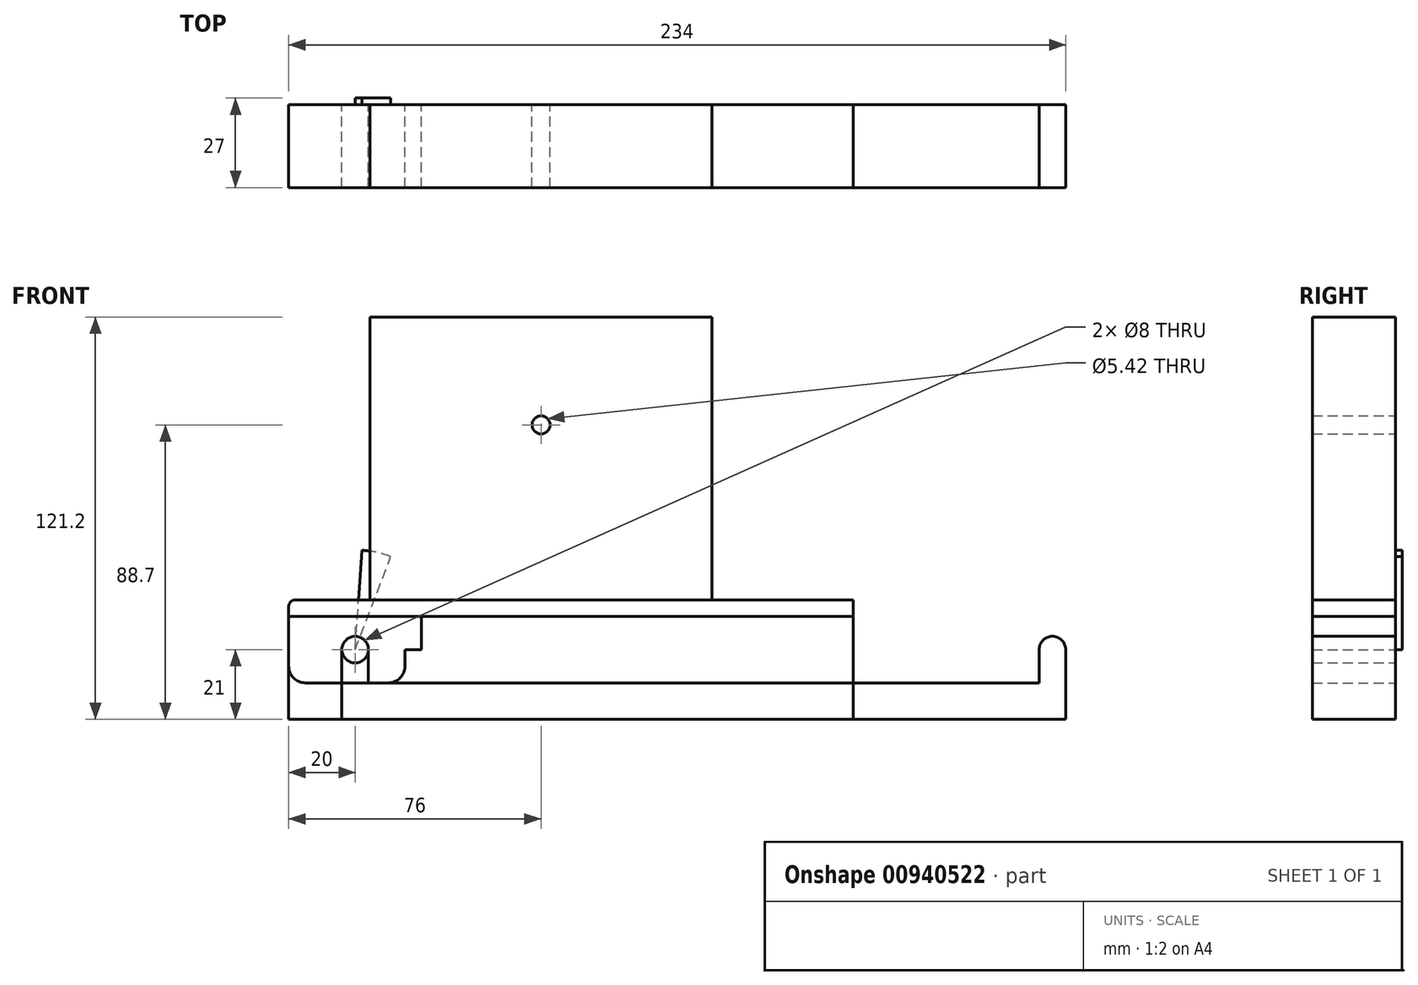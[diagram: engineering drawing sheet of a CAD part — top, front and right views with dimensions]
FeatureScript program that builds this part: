
annotation { "Feature Type Name" : "Feature", "Feature Type Description" : "" }
export const myFeature = defineFeature(function(context is Context, id is Id, definition is map)
    precondition{}
    {
        {
            var Q0;
            Q0=qCreatedBy(makeId("Front.planeOp"),FACE);
            var sketch = newSketch(context, id + "F0", { "sketchPlane" : qUnion([Q0])});
            skLineSegment(sketch, "E0.bottom", {"start": v(-20, 10) * mm, "end": v(150, 10) * mm});
            skLineSegment(sketch, "E0.top", {"start": v(-20, -21) * mm, "end": v(150, -21) * mm});
            skLineSegment(sketch, "E0.left", {"start": v(-20, 10) * mm, "end": v(-20, -21) * mm});
            skLineSegment(sketch, "E0.right", {"start": v(150, 10) * mm, "end": v(150, -21) * mm});
            skCircle(sketch, "E1", {"center": v(0, 0) * mm, "radius": 4 * mm});
            skSolve(sketch);
        }
        {
            var Q0;
            Q0 = qSketchRegion(id + "F0", true);
            extrude(context, id + "F1", {"entities" : qUnion([Q0]), "depth" : 25 * mm, "offsetDistance" : 25 * mm});
        }
        {
            var Q0;
            Q0=qCreatedBy(makeId("Front.planeOp"),FACE);
            var sketch = newSketch(context, id + "F2", { "sketchPlane" : qUnion([Q0])});
            skCircle(sketch, "E2", {"center": v(0, 0) * mm, "radius": 4 * mm});
            skLineSegment(sketch, "E3.0", {"start": v(20, 10) * mm, "end": v(150, 10) * mm});
            skLineSegment(sketch, "E4.0", {"start": v(-18, 15) * mm, "end": v(150, 15) * mm});
            skLineSegment(sketch, "E5", {"start": v(-20, 13) * mm, "end": v(-20, -5) * mm});
            skLineSegment(sketch, "E6", {"start": v(-15, -10) * mm, "end": v(10, -10) * mm});
            skLineSegment(sketch, "E7", {"start": v(20, 0) * mm, "end": v(20, 10) * mm});
            skLineSegment(sketch, "E8", {"start": v(150, 15) * mm, "end": v(150, 10) * mm});
            skPoint(sketch, "E9.orphan", {"position": v(-20, 10) * mm});
            skPoint(sketch, "E10.visualSharp", {"position": v(-20, -10) * mm});
            skArc(sketch, "E10.filletArc", {"start": v(-20, -5) * mm, "mid": v(-18.54, -8.54) * mm, "end": v(-15, -10) * mm});
            skPoint(sketch, "E11.visualSharp", {"position": v(20, -10) * mm});
            skPoint(sketch, "E12.visualSharp", {"position": v(-20, 15) * mm});
            skArc(sketch, "E12.filletArc", {"start": v(-18, 15) * mm, "mid": v(-19.41, 14.41) * mm, "end": v(-20, 13) * mm});
            skLineSegment(sketch, "E13", {"start": v(20, 0) * mm, "end": v(15, 0) * mm});
            skLineSegment(sketch, "E14", {"start": v(15, 0) * mm, "end": v(15, -5) * mm});
            skArc(sketch, "E15.filletArc", {"start": v(10, -10) * mm, "mid": v(13.54, -8.54) * mm, "end": v(15, -5) * mm});
            skSolve(sketch);
        }
        {
            var Q0;
            Q0 = qSketchRegion(id + "F2", true);
            extrude(context, id + "F3", {"entities" : qUnion([Q0]), "depth" : 25 * mm, "offsetDistance" : 25 * mm});
        }
        {
            var Q0;
            Q0=qCreatedBy(makeId("Front.planeOp"),FACE);
            var sketch = newSketch(context, id + "F4", { "sketchPlane" : qUnion([Q0])});
            skLineSegment(sketch, "E16.bottom", {"start": v(4.5, 15) * mm, "end": v(107.5, 15) * mm});
            skLineSegment(sketch, "E16.top", {"start": v(4.5, 100.2) * mm, "end": v(107.5, 100.2) * mm});
            skLineSegment(sketch, "E16.left", {"start": v(4.5, 15) * mm, "end": v(4.5, 100.2) * mm});
            skLineSegment(sketch, "E16.right", {"start": v(107.5, 15) * mm, "end": v(107.5, 100.2) * mm});
            skLineSegment(sketch, "E17", {"start": v(56, 15) * mm, "end": v(56, 81.83) * mm, "construction": true});
            skLineSegment(sketch, "E18", {"start": v(38.86, 67.7) * mm, "end": v(102.85, 67.7) * mm, "construction": true});
            skCircle(sketch, "E19", {"center": v(56, 67.7) * mm, "radius": 2.71 * mm});
            skSolve(sketch);
        }
        {
            var Q0;
            Q0 = qSketchRegion(id + "F4", true);
            extrude(context, id + "F5", {"entities" : qUnion([Q0]), "depth" : 25 * mm, "offsetDistance" : 25 * mm});
        }
        {
            var Q0;
            Q0=qCreatedBy(makeId("Front.planeOp"),FACE);
            var sketch = newSketch(context, id + "F6", { "sketchPlane" : qUnion([Q0])});
            skCircle(sketch, "E20.0", {"center": v(56, 67.7) * mm, "radius": 2.71 * mm});
            skArc(sketch, "E21", {"start": v(19.83, 22.52) * mm, "mid": v(-5.71, 29.45) * mm, "end": v(-26.8, 13.47) * mm});
            skLineSegment(sketch, "E22", {"start": v(0, 0) * mm, "end": v(2.1, 29.93) * mm});
            skLineSegment(sketch, "E23", {"start": v(0, 0) * mm, "end": v(10.75, 28) * mm});
            skLineSegment(sketch, "E24", {"start": v(56, 67.7) * mm, "end": v(56, 0) * mm, "construction": true});
            skSolve(sketch);
        }
        {
            var Q0;
            Q0 = qSketchRegion(id + "F6", true);
            extrude(context, id + "F7", {"entities" : qUnion([Q0]), "oppositeDirection" : true, "depth" : 2 * mm, "offsetDistance" : 25 * mm});
        }
        {
            var Q0;
            Q0=qCreatedBy(makeId("Front.planeOp"),FACE);
            var sketch = newSketch(context, id + "F8", { "sketchPlane" : qUnion([Q0])});
            skArc(sketch, "E25.0", {"start": v(4, 0) * mm, "mid": v(0, 4) * mm, "end": v(-4, 0) * mm});
            skLineSegment(sketch, "E26.0", {"start": v(-20, -21) * mm, "end": v(214, -21) * mm});
            skLineSegment(sketch, "E27", {"start": v(-4, 0) * mm, "end": v(-4, -21) * mm});
            skLineSegment(sketch, "E28.0", {"start": v(206, 0) * mm, "end": v(206, -10) * mm});
            skArc(sketch, "E29.0", {"start": v(214, 0) * mm, "mid": v(210, 4) * mm, "end": v(206, 0) * mm});
            skPoint(sketch, "E30.orphan", {"position": v(150, -21) * mm});
            skLineSegment(sketch, "E31", {"start": v(4, 0) * mm, "end": v(4, -10) * mm});
            skLineSegment(sketch, "E32", {"start": v(4, -10) * mm, "end": v(206, -10) * mm});
            skLineSegment(sketch, "E33", {"start": v(214, 0) * mm, "end": v(214, -21) * mm});
            skSolve(sketch);
        }
        {
            var Q0;
            Q0 = qSketchRegion(id + "F8", true);
            extrude(context, id + "F9", {"entities" : qUnion([Q0]), "depth" : 25 * mm, "offsetDistance" : 25 * mm});
        }
        {
            var Q0;
            Q0=makeQuery(id+"F7.opExtrude","SWEPT_BODY",BODY,{"disambiguationData":[OSD([sQuery(id+"F6.wireOp",EDGE,"E20.0")])]});
            deleteBodies(context, id + "F10", {"entities" : qUnion([Q0])});
        }
    });
